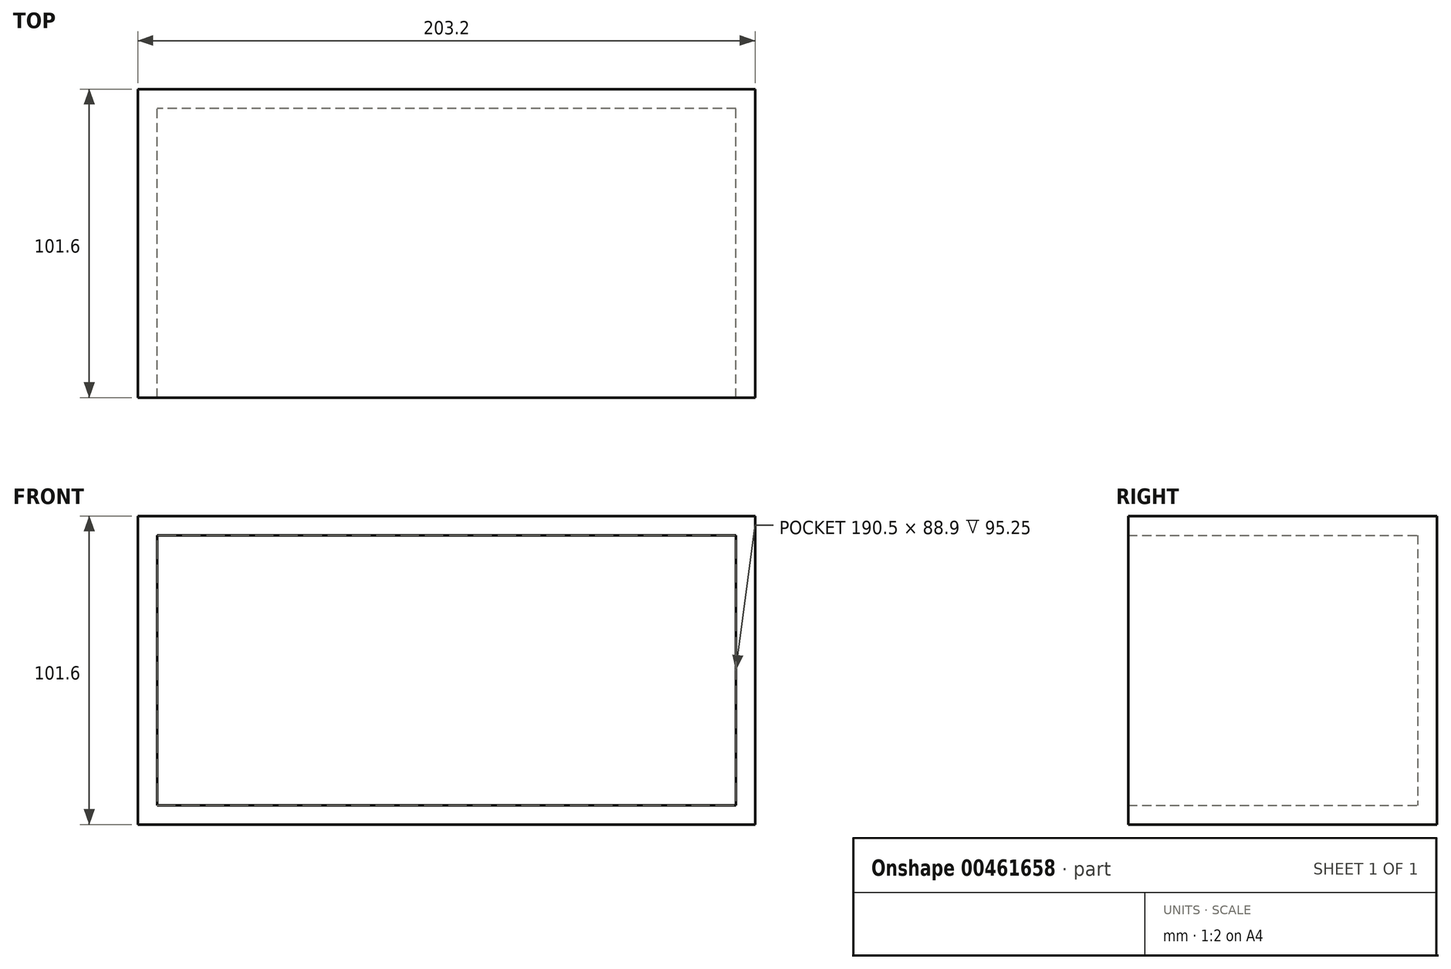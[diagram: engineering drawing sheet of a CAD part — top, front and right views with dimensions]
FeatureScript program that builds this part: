
annotation { "Feature Type Name" : "Feature", "Feature Type Description" : "" }
export const myFeature = defineFeature(function(context is Context, id is Id, definition is map)
    precondition{}
    {
        {
            var Q0;
            Q0=qCreatedBy(makeId("Top.planeOp"),FACE);
            var sketch = newSketch(context, id + "F0", { "sketchPlane" : qUnion([Q0])});
            skLineSegment(sketch, "E0.bottom", {"start": v(101.6, -50.8) * mm, "end": v(-101.6, -50.8) * mm});
            skLineSegment(sketch, "E0.top", {"start": v(101.6, 50.8) * mm, "end": v(-101.6, 50.8) * mm});
            skLineSegment(sketch, "E0.left", {"start": v(101.6, -50.8) * mm, "end": v(101.6, 50.8) * mm});
            skLineSegment(sketch, "E0.right", {"start": v(-101.6, -50.8) * mm, "end": v(-101.6, 50.8) * mm});
            skPoint(sketch, "E0.middle", {"position": v(0, 0) * mm});
            skSolve(sketch);
        }
        {
            var Q0;
            Q0 = qSketchRegion(id + "F0", true);
            extrude(context, id + "F1", {"entities" : qUnion([Q0]), "depth" : 101.6 * mm});
        }
        {
            var Q0;
            Q0=makeQuery(id+"F1.opExtrude","SWEPT_FACE",FACE,{"disambiguationData":[OSD([sQuery(id+"F0.wireOp",EDGE,"E0.bottom")])]});
            shell(context, id + "F2", {"entities" : qUnion([Q0]), "thickness" : 6.35 * mm});
        }
    });
